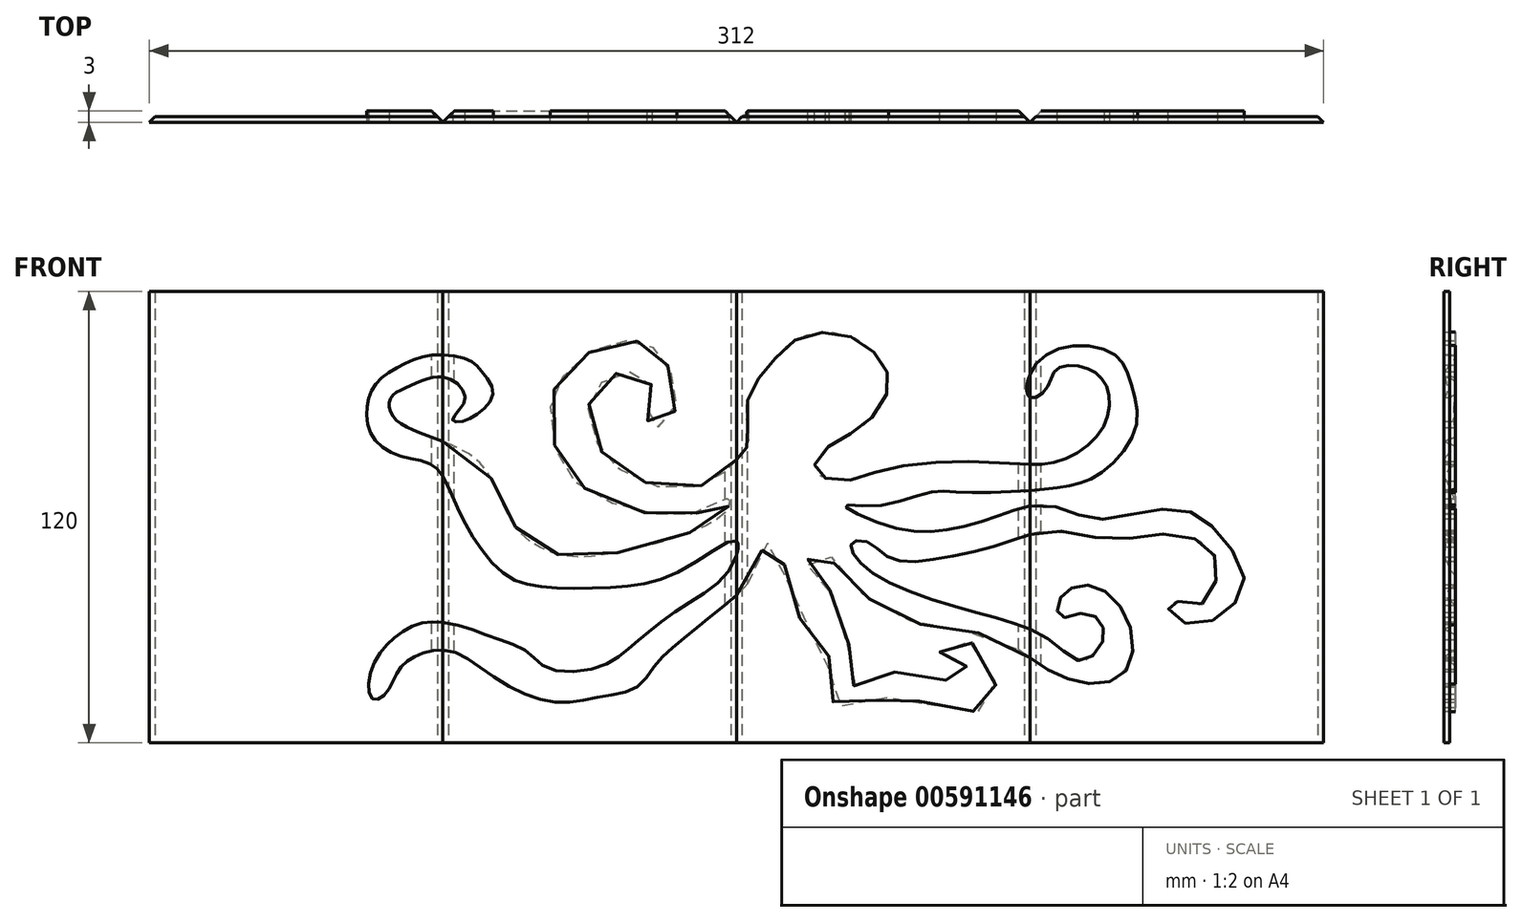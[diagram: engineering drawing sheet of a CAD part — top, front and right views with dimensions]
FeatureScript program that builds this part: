
annotation { "Feature Type Name" : "Feature", "Feature Type Description" : "" }
export const myFeature = defineFeature(function(context is Context, id is Id, definition is map)
    precondition{}
    {
        {
            var Q0;
            Q0=qCreatedBy(makeId("Top.planeOp"),FACE);
            var sketch = newSketch(context, id + "F0", { "sketchPlane" : qUnion([Q0])});
            skLineSegment(sketch, "E0", {"start": v(-73.98, 9.57) * mm, "end": v(1.02, 9.57) * mm});
            skLineSegment(sketch, "E1", {"start": v(1.02, 9.57) * mm, "end": v(2.52, 8.07) * mm});
            skLineSegment(sketch, "E2", {"start": v(2.52, 8.07) * mm, "end": v(-75.48, 8.07) * mm});
            skLineSegment(sketch, "E3", {"start": v(-75.48, 8.07) * mm, "end": v(-73.98, 9.57) * mm});
            skLineSegment(sketch, "E4.1.0.0", {"start": v(4.02, 9.57) * mm, "end": v(79.02, 9.57) * mm});
            skLineSegment(sketch, "E4.1.0.1", {"start": v(80.52, 8.07) * mm, "end": v(2.52, 8.07) * mm});
            skLineSegment(sketch, "E4.1.0.2", {"start": v(79.02, 9.57) * mm, "end": v(80.52, 8.07) * mm});
            skLineSegment(sketch, "E4.1.0.3", {"start": v(2.52, 8.07) * mm, "end": v(4.02, 9.57) * mm});
            skLineSegment(sketch, "E4.2.0.0", {"start": v(82.02, 9.57) * mm, "end": v(157.02, 9.57) * mm});
            skLineSegment(sketch, "E4.2.0.1", {"start": v(158.52, 8.07) * mm, "end": v(80.52, 8.07) * mm});
            skLineSegment(sketch, "E4.2.0.2", {"start": v(157.02, 9.57) * mm, "end": v(158.52, 8.07) * mm});
            skLineSegment(sketch, "E4.2.0.3", {"start": v(80.52, 8.07) * mm, "end": v(82.02, 9.57) * mm});
            skLineSegment(sketch, "E4.3.0.0", {"start": v(160.02, 9.57) * mm, "end": v(235.02, 9.57) * mm});
            skLineSegment(sketch, "E4.3.0.1", {"start": v(236.52, 8.07) * mm, "end": v(158.52, 8.07) * mm});
            skLineSegment(sketch, "E4.3.0.2", {"start": v(235.02, 9.57) * mm, "end": v(236.52, 8.07) * mm});
            skLineSegment(sketch, "E4.3.0.3", {"start": v(158.52, 8.07) * mm, "end": v(160.02, 9.57) * mm});
            skLineSegment(sketch, "E4.direction1", {"start": v(-75.48, 8.07) * mm, "end": v(2.52, 8.07) * mm, "construction": true});
            skSolve(sketch);
        }
        {
            var Q0;
            Q0=makeQuery(id+"F0.imprint","IMPRINT",FACE,{"disambiguationData":[TD([[makeQuery(id+"F0.imprint","IMPRINT",EDGE,{"derivedFrom":sQuery(id+"F0.wireOp",EDGE,"E0")}),-1.0]])]});
            extrude(context, id + "F1", {"entities" : qUnion([Q0]), "depth" : 120 * mm, "offsetDistance" : 25 * mm});
        }
        {
            var Q0;
            Q0=makeQuery(id+"F0.imprint","IMPRINT",FACE,{"disambiguationData":[TD([[makeQuery(id+"F0.imprint","IMPRINT",EDGE,{"derivedFrom":sQuery(id+"F0.wireOp",EDGE,"E4.1.0.0")}),-1.0]])]});
            extrude(context, id + "F2", {"entities" : qUnion([Q0]), "depth" : 120 * mm, "offsetDistance" : 25 * mm});
        }
        {
            var Q0;
            Q0=makeQuery(id+"F0.imprint","IMPRINT",FACE,{"disambiguationData":[TD([[makeQuery(id+"F0.imprint","IMPRINT",EDGE,{"derivedFrom":sQuery(id+"F0.wireOp",EDGE,"E4.2.0.0")}),-1.0]])]});
            extrude(context, id + "F3", {"entities" : qUnion([Q0]), "depth" : 120 * mm, "offsetDistance" : 25 * mm});
        }
        {
            var Q0;
            Q0=makeQuery(id+"F0.imprint","IMPRINT",FACE,{"disambiguationData":[TD([[makeQuery(id+"F0.imprint","IMPRINT",EDGE,{"derivedFrom":sQuery(id+"F0.wireOp",EDGE,"E4.3.0.0")}),-1.0]])]});
            extrude(context, id + "F4", {"entities" : qUnion([Q0]), "depth" : 120 * mm, "offsetDistance" : 25 * mm});
        }
        {
            var Q0;
            Q0=makeQuery(id+"F3.opExtrude","SWEPT_FACE",FACE,{"disambiguationData":[OSD([sQuery(id+"F0.wireOp",EDGE,"E4.2.0.1")])]});
            var sketch = newSketch(context, id + "F5", { "sketchPlane" : qUnion([Q0])});
            skPoint(sketch, "E5.174.internal.snap0", {"position": v(158.52, 60) * mm});
            skFitSpline(sketch, "E5", {"points": [v(83.62, 79.52) * mm, v(82.23, 77.34) * mm, v(78.27, 72.79) * mm, v(73.72, 69.42) * mm, v(65.4, 67.24) * mm, v(54.5, 70.02) * mm, v(46.38, 75.17) * mm, v(42.82, 81.7) * mm, v(41.23, 89.63) * mm, v(43.8, 94.78) * mm, v(48.36, 98.14) * mm, v(54.3, 98.34) * mm, v(57.67, 95.77) * mm, v(58.07, 91.21) * mm, v(56.88, 87.05) * mm, v(57.67, 84.28) * mm, v(61.83, 84.67) * mm, v(64.6, 90.22) * mm, v(63.61, 97.35) * mm, v(60.64, 102.9) * mm, v(56.68, 106.07) * mm, v(51.14, 106.86) * mm, v(42.82, 104.68) * mm, v(35.49, 98.54) * mm, v(31.72, 93) * mm, v(31.33, 83.29) * mm, v(34.9, 72.4) * mm, v(41.23, 67.04) * mm, v(54.1, 61.5) * mm, v(63.81, 60.9) * mm, v(71.93, 61.7) * mm, v(78.27, 64.87) * mm, v(78.07, 62.1) * mm, v(73.12, 58.13) * mm, v(63.22, 54.17) * mm, v(44.4, 49.81) * mm, v(34.3, 49.81) * mm, v(26.18, 53.18) * mm, v(20.83, 58.92) * mm, v(16.47, 67.84) * mm, v(10.73, 75.96) * mm, v(-2.74, 82.1) * mm, v(-10.87, 86.96) * mm, v(-11.39, 91.6) * mm, v(-7.34, 94.43) * mm, v(0, 97.18) * mm, v(5.4, 96.18) * mm, v(8.39, 91.93) * mm, v(6.64, 88.19) * mm, v(5.14, 85.7) * mm, v(7.64, 85.44) * mm, v(12.63, 88.19) * mm, v(15.88, 93.18) * mm, v(12.63, 98.93) * mm, v(9.59, 101.74) * mm, v(0, 103.13) * mm, v(-8.62, 100.35) * mm, v(-15.15, 95.6) * mm, v(-17.53, 89.67) * mm, v(-16.54, 82.15) * mm, v(-9.41, 76.4) * mm, v(0, 73.64) * mm, v(5.03, 65.52) * mm, v(9.98, 55.63) * mm, v(19.28, 44.54) * mm, v(30.17, 41.38) * mm, v(48.58, 41.38) * mm, v(66.39, 46.13) * mm, v(80.52, 53.65) * mm, v(78.4, 45.58) * mm, v(68.32, 37.53) * mm, v(57.42, 29.71) * mm, v(51.37, 24.58) * mm, v(43.73, 20.04) * mm, v(30.36, 19.8) * mm, v(25.1, 24.1) * mm, v(17.46, 27.45) * mm, v(8.15, 30.79) * mm, v(-2.12, 31.98) * mm, v(-10.95, 27.45) * mm, v(-16.68, 18.61) * mm, v(-16.2, 11.69) * mm, v(-12.86, 12.88) * mm, v(-9.52, 18.85) * mm, v(-4.98, 22.9) * mm, v(3.61, 24.58) * mm, v(11.73, 20.52) * mm, v(24.39, 12.88) * mm, v(35.61, 10.73) * mm, v(45.16, 12.4) * mm, v(54, 14.8) * mm, v(59.49, 21.24) * mm, v(66.41, 27.69) * mm, v(77.64, 36.76) * mm, v(85.04, 44.64) * mm, v(87.67, 51.8) * mm, v(89.82, 53.24) * mm, v(92.92, 48.7) * mm, v(95.07, 37) * mm, v(99.6, 31.03) * mm, v(104.86, 25.06) * mm, v(104.14, 16.7) * mm, v(106.05, 10.97) * mm, v(114.65, 9.54) * mm, v(120.86, 12.16) * mm, v(125.63, 12.64) * mm, v(130.89, 10.25) * mm, v(141.15, 8.58) * mm, v(148.08, 9.06) * mm, v(149.51, 14.07) * mm, v(147.84, 20.76) * mm, v(142.35, 26.97) * mm, v(137.1, 26.5) * mm, v(134.7, 24.58) * mm, v(134.95, 22.43) * mm, v(139.48, 22.43) * mm, v(142.11, 18.13) * mm, v(140.44, 15.03) * mm, v(134.23, 17.66) * mm, v(125.16, 19.33) * mm, v(118.23, 16.7) * mm, v(112.74, 14.8) * mm, v(109.4, 18.37) * mm, v(110.35, 25.06) * mm, v(108.2, 35.09) * mm, v(102.95, 43.2) * mm, v(99.84, 45.12) * mm, v(100.56, 51.09) * mm, v(104.14, 51.33) * mm, v(107.25, 46.31) * mm, v(112.98, 40.34) * mm, v(120.86, 35.09) * mm, v(131.36, 31.03) * mm, v(142.35, 29.6) * mm, v(152.38, 26.73) * mm, v(161.93, 20.28) * mm, v(173.87, 15.75) * mm, v(183.9, 18.97) * mm, v(185.01, 31.44) * mm, v(176.98, 41.13) * mm, v(169.5, 41.13) * mm, v(165.9, 36.98) * mm, v(166.73, 33.37) * mm, v(173.1, 34.48) * mm, v(177.53, 31.71) * mm, v(177.81, 26.73) * mm, v(172.55, 21.74) * mm, v(165.35, 26.17) * mm, v(155.38, 31.44) * mm, v(136.82, 36.7) * mm, v(116.88, 45) * mm, v(111.34, 50.82) * mm, v(111.34, 53.32) * mm, v(115.5, 53.32) * mm, v(121.31, 49.16) * mm, v(132.11, 48.6) * mm, v(150.67, 52.76) * mm, v(164.8, 56.36) * mm, v(180.3, 54.15) * mm, v(195.81, 55.53) * mm, v(206.61, 51.38) * mm, v(208, 43.34) * mm, v(202.74, 36.42) * mm, v(195.81, 37.8) * mm, v(195.81, 34.48) * mm, v(203.01, 31.44) * mm, v(212.43, 36.42) * mm, v(215.2, 45.28) * mm, v(207.72, 56.64) * mm, v(200.52, 61.62) * mm, v(188.06, 61.35) * mm, v(176.98, 59.4) * mm, v(169.23, 61.35) * mm, v(161.2, 63.29) * mm, v(149, 60) * mm, v(134.88, 56.36) * mm, v(120.48, 57.75) * mm, v(109.4, 63) * mm, v(117.71, 63) * mm, v(132.11, 66.6) * mm, v(139.31, 66.6) * mm, v(155.93, 66.89) * mm, v(168.67, 68.27) * mm, v(177.26, 71.6) * mm, v(186.67, 83.78) * mm, v(185.29, 95.69) * mm, v(181.13, 103.17) * mm, v(167.29, 105.1) * mm, v(158.52, 97.9) * mm, v(158.52, 91.81) * mm, v(162.86, 94.03) * mm, v(165.62, 99.29) * mm, v(173.66, 99.57) * mm, v(178.92, 94.58) * mm, v(178.09, 84.06) * mm, v(166.18, 74.92) * mm, v(151.5, 74.36) * mm, v(135.16, 74.64) * mm, v(118.82, 72.42) * mm, v(108.57, 69.66) * mm, v(101.37, 72.42) * mm, v(104.7, 78.52) * mm, v(113.84, 84.06) * mm, v(120.76, 93.75) * mm, v(119.1, 101.5) * mm, v(109.68, 108.43) * mm, v(96.66, 107.32) * mm, v(88.36, 99.29) * mm, v(83.37, 90.43) * mm, v(83.62, 79.52) * mm]});
            skSolve(sketch);
        }
        {
            var Q0;
            Q0 = qSketchRegion(id + "F5", true);
            extrude(context, id + "F6", {"entities" : qUnion([Q0]), "oppositeDirection" : true, "depth" : 3 * mm, "offsetDistance" : 25 * mm});
        }
        {
            var Q0;
            Q0=makeQuery(id+"F2.opExtrude","CAP_FACE",FACE,{"disambiguationData":[OSD([sQuery(id+"F0.wireOp",EDGE,"E4.1.0.0"),sQuery(id+"F0.wireOp",EDGE,"E4.1.0.1"),sQuery(id+"F0.wireOp",EDGE,"E4.1.0.2"),sQuery(id+"F0.wireOp",EDGE,"E4.1.0.3")])],"isStart":false});
            var sketch = newSketch(context, id + "F7", { "sketchPlane" : qUnion([Q0])});
            skLineSegment(sketch, "E6", {"start": v(2.52, 8.07) * mm, "end": v(7.01, 12.56) * mm});
            skLineSegment(sketch, "E7", {"start": v(2.52, 8.07) * mm, "end": v(-1.98, 12.56) * mm});
            skLineSegment(sketch, "E8", {"start": v(-1.98, 12.56) * mm, "end": v(7.01, 12.56) * mm});
            skLineSegment(sketch, "E9.1.0.0", {"start": v(76.02, 12.56) * mm, "end": v(85.01, 12.56) * mm});
            skLineSegment(sketch, "E9.1.0.1", {"start": v(80.52, 8.07) * mm, "end": v(76.02, 12.56) * mm});
            skLineSegment(sketch, "E9.1.0.2", {"start": v(80.52, 8.07) * mm, "end": v(85.01, 12.56) * mm});
            skLineSegment(sketch, "E9.2.0.0", {"start": v(154.02, 12.56) * mm, "end": v(163.01, 12.56) * mm});
            skLineSegment(sketch, "E9.2.0.1", {"start": v(158.52, 8.07) * mm, "end": v(154.02, 12.56) * mm});
            skLineSegment(sketch, "E9.2.0.2", {"start": v(158.52, 8.07) * mm, "end": v(163.01, 12.56) * mm});
            skLineSegment(sketch, "E9.direction1", {"start": v(2.52, 8.07) * mm, "end": v(80.52, 8.07) * mm, "construction": true});
            skSolve(sketch);
        }
        {
            var Q0;
            {var subQ0=sQuery(id+"F7.wireOp",EDGE,"E7");Q0=makeQuery(id+"F7.imprint","IMPRINT",FACE,{"disambiguationData":[TD([[makeQuery(id+"F7.imprint","IMPRINT",EDGE,{"derivedFrom":subQ0}),-1.0]])]});}
            var Q1;
            {var subQ0=sQuery(id+"F7.wireOp",EDGE,"E9.1.0.0");Q1=makeQuery(id+"F7.imprint","IMPRINT",FACE,{"disambiguationData":[TD([[makeQuery(id+"F7.imprint","IMPRINT",EDGE,{"derivedFrom":subQ0}),-1.0]])]});}
            var Q2;
            Q2=makeQuery(id+"F7.imprint","IMPRINT",FACE,{"disambiguationData":[TD([[makeQuery(id+"F7.imprint","IMPRINT",EDGE,{"derivedFrom":sQuery(id+"F7.wireOp",EDGE,"E9.2.0.0")}),-1.0]])]});
            extrude(context, id + "F8", {"entities" : qUnion([Q0, Q1, Q2]), "operationType" : NewBodyOperationType.REMOVE, "endBound" : BoundingType.THROUGH_ALL, "oppositeDirection" : true, "depth" : 25 * mm, "offsetDistance" : 25 * mm});
        }
    });
